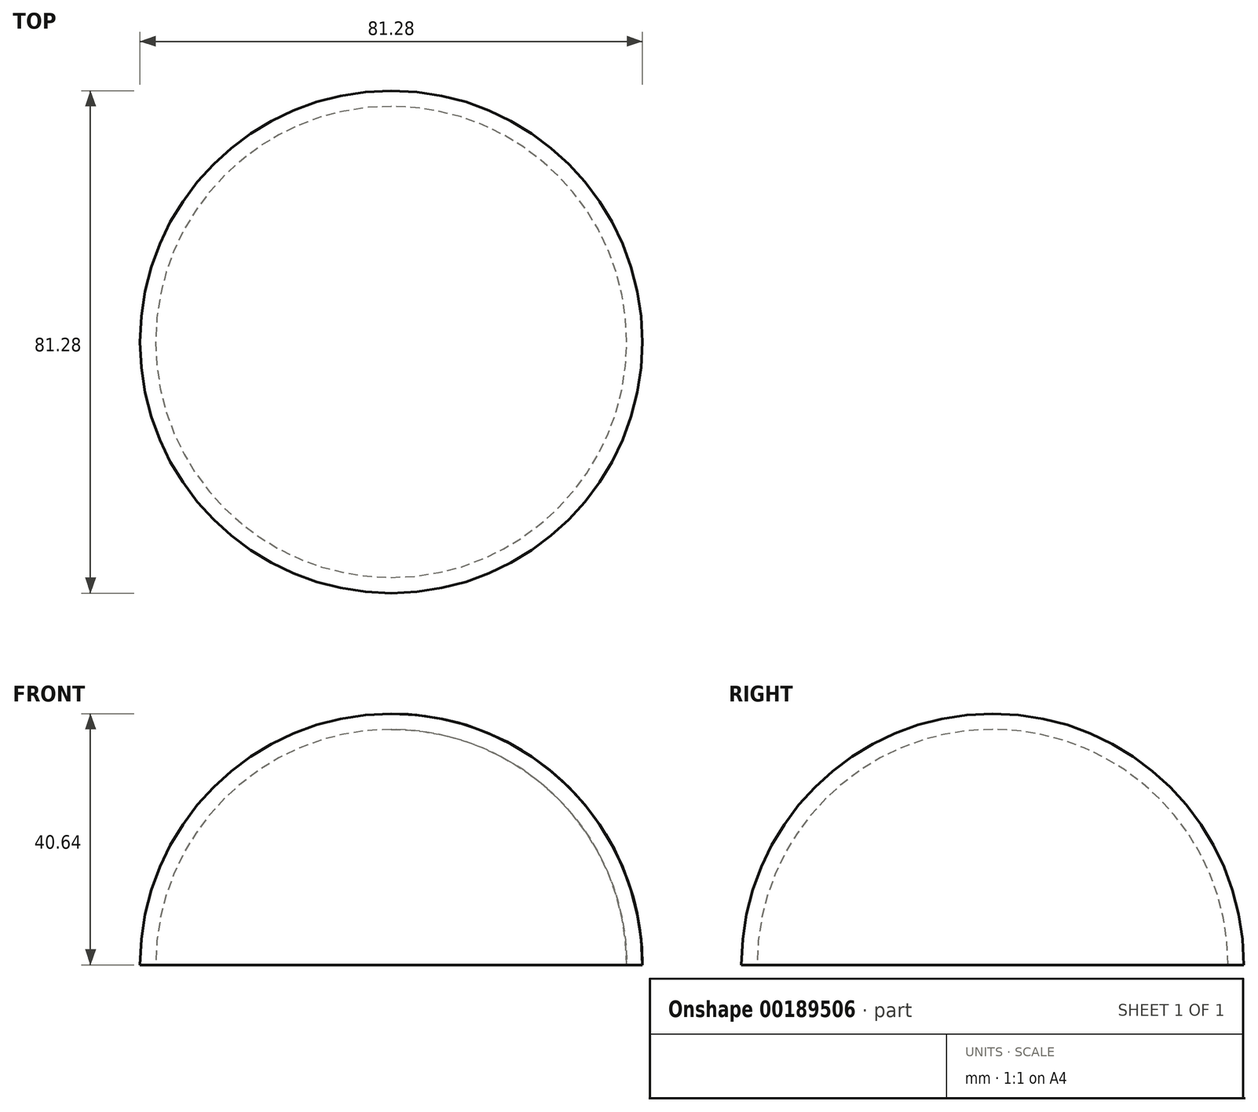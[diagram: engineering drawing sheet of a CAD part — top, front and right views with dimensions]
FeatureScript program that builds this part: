
annotation { "Feature Type Name" : "Feature", "Feature Type Description" : "" }
export const myFeature = defineFeature(function(context is Context, id is Id, definition is map)
    precondition{}
    {
        {
            var Q0;
            Q0=qCreatedBy(makeId("Front.planeOp"),FACE);
            var sketch = newSketch(context, id + "F0", { "sketchPlane" : qUnion([Q0])});
            skLineSegment(sketch, "E0", {"start": v(0, 0) * mm, "end": v(54.61, 0) * mm, "construction": true});
            skLineSegment(sketch, "E1", {"start": v(0, 0) * mm, "end": v(0, 89.94) * mm, "construction": true});
            skSolve(sketch);
        }
        {
            var Q0;
            Q0=qCreatedBy(makeId("Front.planeOp"),FACE);
            var sketch = newSketch(context, id + "F1", { "sketchPlane" : qUnion([Q0])});
            skArc(sketch, "E2", {"start": v(38.1, 0) * mm, "mid": v(26.94, 26.94) * mm, "end": v(0, 38.1) * mm});
            skArc(sketch, "E3", {"start": v(40.64, 0) * mm, "mid": v(28.74, 28.74) * mm, "end": v(0, 40.64) * mm});
            skLineSegment(sketch, "E4", {"start": v(38.1, 0) * mm, "end": v(40.64, 0) * mm});
            skLineSegment(sketch, "E5", {"start": v(0, 38.1) * mm, "end": v(0, 40.64) * mm});
            skSolve(sketch);
        }
        {
            var Q0;
            Q0=makeQuery(id+"F1.imprint","IMPRINT",FACE,{"disambiguationData":[TD([[makeQuery(id+"F1.imprint","IMPRINT",EDGE,{"derivedFrom":sQuery(id+"F1.wireOp",EDGE,"E2")}),-1.0]])]});
            var Q1;
            Q1=sQuery(id+"F0.wireOp",EDGE,"E1");
            revolve(context, id + "F2", {"entities" : qUnion([Q0]), "axis" : qUnion([Q1]), "revolveType" : RevolveType.FULL});
        }
    });
